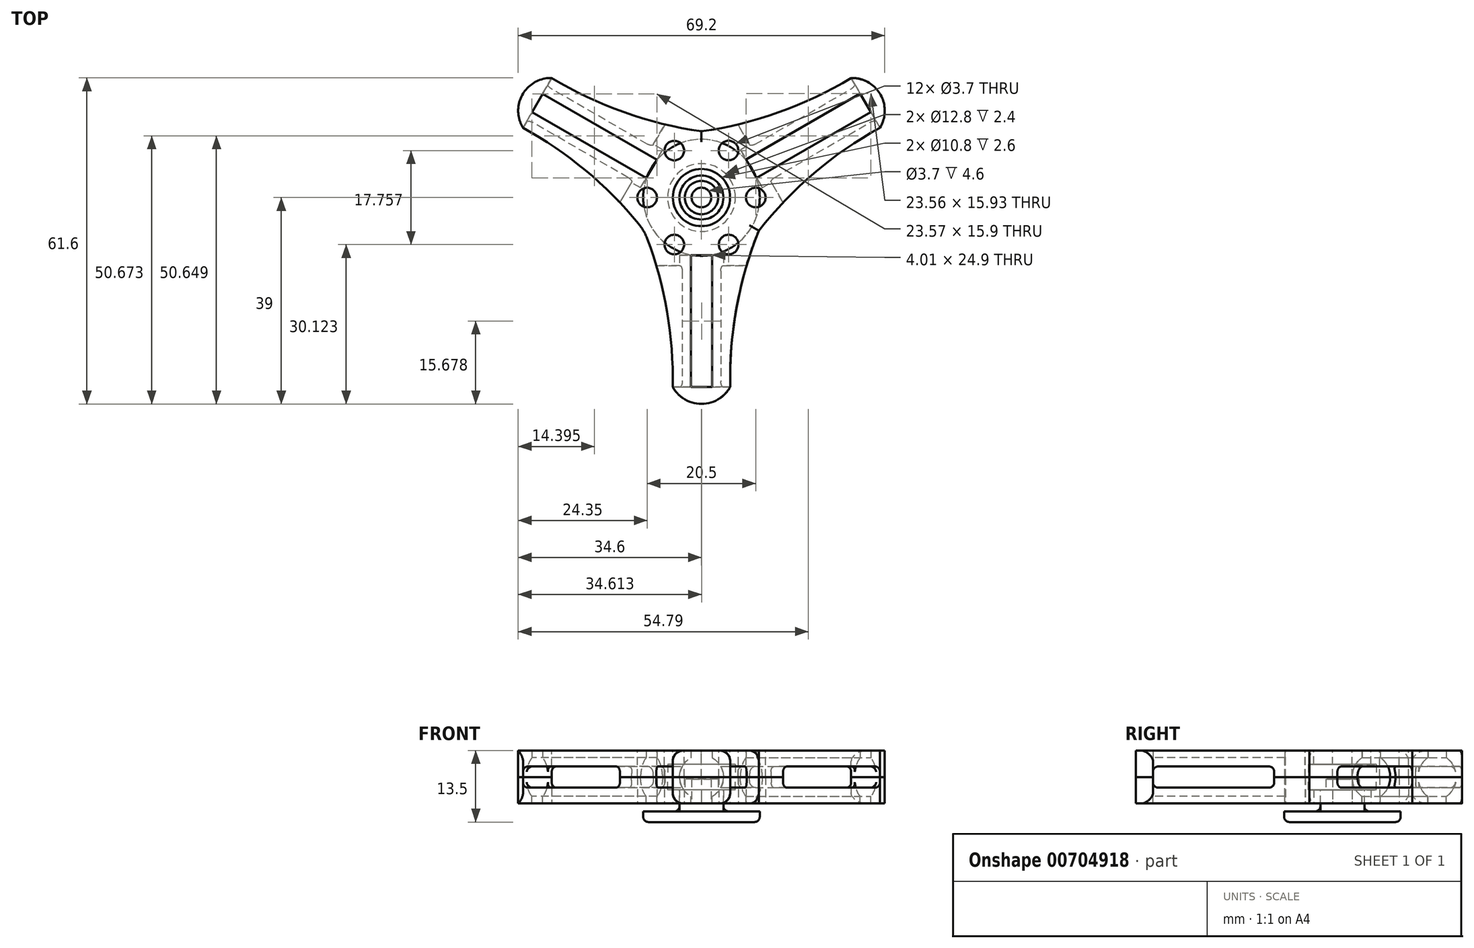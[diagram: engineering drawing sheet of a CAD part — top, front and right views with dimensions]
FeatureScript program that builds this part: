
annotation { "Feature Type Name" : "Feature", "Feature Type Description" : "" }
export const myFeature = defineFeature(function(context is Context, id is Id, definition is map)
    precondition{}
    {
        {
            var Q0;
            Q0=qCreatedBy(makeId("Top.planeOp"),FACE);
            var sketch = newSketch(context, id + "F0", { "sketchPlane" : qUnion([Q0])});
            skCircle(sketch, "E0", {"center": v(0, 0) * mm, "radius": 6.4 * mm, "construction": true});
            skArc(sketch, "E1", {"start": v(0, 12.5) * mm, "mid": v(-10.83, -6.25) * mm, "end": v(10.83, -6.25) * mm, "construction": true});
            skLineSegment(sketch, "E2", {"start": v(0, 12.5) * mm, "end": v(0, 39.67) * mm, "construction": true});
            skLineSegment(sketch, "E3", {"start": v(0, 0) * mm, "end": v(33.28, -19.21) * mm, "construction": true});
            skLineSegment(sketch, "E4", {"start": v(0, 0) * mm, "end": v(33.77, 19.5) * mm, "construction": true});
            skCircle(sketch, "E5", {"center": v(13, 7.5) * mm, "radius": 4.15 * mm, "construction": true});
            skCircle(sketch, "E6", {"center": v(20.2, 11.66) * mm, "radius": 4.15 * mm, "construction": true});
            skCircle(sketch, "E7", {"center": v(27.38, 15.8) * mm, "radius": 4.15 * mm, "construction": true});
            skLineSegment(sketch, "E8", {"start": v(33.77, 19.5) * mm, "end": v(54.08, 31.22) * mm, "construction": true});
            skPoint(sketch, "E9", {"position": v(30.98, 17.88) * mm});
            skLineSegment(sketch, "E10", {"start": v(28.26, 22.59) * mm, "end": v(33.7, 13.18) * mm});
            skArc(sketch, "E11", {"start": v(0, 12.5) * mm, "mid": v(14.64, 16.12) * mm, "end": v(28.26, 22.59) * mm});
            skArc(sketch, "E12.MirrorCS", {"start": v(10.83, -6.25) * mm, "mid": v(21.28, 4.62) * mm, "end": v(33.7, 13.18) * mm});
            skArc(sketch, "E13", {"start": v(0, 12.5) * mm, "mid": v(-10.83, -6.25) * mm, "end": v(10.83, -6.25) * mm});
            skLineSegment(sketch, "E14", {"start": v(0, 0) * mm, "end": v(6.65, 11.52) * mm, "construction": true});
            skLineSegment(sketch, "E15", {"start": v(0, 0) * mm, "end": v(12.69, 0) * mm, "construction": true});
            skCircle(sketch, "E16", {"center": v(5.12, 8.88) * mm, "radius": 1.85 * mm});
            skCircle(sketch, "E17.MirrorC", {"center": v(10.25, 0) * mm, "radius": 1.85 * mm});
            skCircle(sketch, "E18", {"center": v(0, 0) * mm, "radius": 5.4 * mm});
            skSolve(sketch);
        }
        {
            var Q0;
            Q0 = qSketchRegion(id + "F0", true);
            extrude(context, id + "F1", {"entities" : qUnion([Q0]), "depth" : 10 * mm, "offsetDistance" : 25 * mm});
        }
        {
            var Q0;
            Q0=makeQuery(id+"F1.opExtrude","SWEPT_FACE",FACE,{"disambiguationData":[OSD([sQuery(id+"F0.wireOp",EDGE,"E10")])]});
            var sketch = newSketch(context, id + "F2", { "sketchPlane" : qUnion([Q0])});
            skLineSegment(sketch, "E19", {"start": v(0, 0) * mm, "end": v(0, 10) * mm, "construction": true});
            skArc(sketch, "E20", {"start": v(-2, 8.64) * mm, "mid": v(-4.15, 5) * mm, "end": v(-2, 1.36) * mm});
            skLineSegment(sketch, "E21.bottom", {"start": v(2, -6.47) * mm, "end": v(-2, -6.47) * mm});
            skLineSegment(sketch, "E21.top", {"start": v(2, 16.47) * mm, "end": v(-2, 16.47) * mm});
            skLineSegment(sketch, "E21.left", {"start": v(2, -6.47) * mm, "end": v(2, 1.36) * mm});
            skLineSegment(sketch, "E21.right", {"start": v(-2, -6.47) * mm, "end": v(-2, 1.36) * mm});
            skArc(sketch, "E22.trimOffspring", {"start": v(2, 1.36) * mm, "mid": v(4.15, 5) * mm, "end": v(2, 8.64) * mm});
            skLineSegment(sketch, "E23.trimOffspring", {"start": v(2, 8.64) * mm, "end": v(2, 16.47) * mm});
            skLineSegment(sketch, "E24.trimOffspring", {"start": v(-2, 8.64) * mm, "end": v(-2, 16.47) * mm});
            skSolve(sketch);
        }
        {
            var Q0;
            Q0 = qSketchRegion(id + "F2", true);
            extrude(context, id + "F3", {"entities" : qUnion([Q0]), "operationType" : NewBodyOperationType.REMOVE, "oppositeDirection" : true, "depth" : 24.9 * mm, "offsetDistance" : 25 * mm});
        }
        {
            var Q0;
            Q0=qCreatedBy(makeId("Top.planeOp"),FACE);
            var sketch = newSketch(context, id + "F4", { "sketchPlane" : qUnion([Q0])});
            skLineSegment(sketch, "E25.0", {"start": v(28.26, 22.59) * mm, "end": v(29.98, 19.62) * mm});
            skLineSegment(sketch, "E25.1", {"start": v(31.98, 16.15) * mm, "end": v(33.7, 13.18) * mm});
            skLineSegment(sketch, "E26", {"start": v(29.98, 19.62) * mm, "end": v(31.98, 16.15) * mm});
            skArc(sketch, "E27", {"start": v(33.7, 13.18) * mm, "mid": v(33.77, 19.5) * mm, "end": v(28.26, 22.59) * mm});
            skSolve(sketch);
        }
        {
            var Q0;
            Q0 = qSketchRegion(id + "F4", true);
            extrude(context, id + "F5", {"entities" : qUnion([Q0]), "operationType" : NewBodyOperationType.ADD, "depth" : 10 * mm, "offsetDistance" : 25 * mm});
        }
        {
            var Q0;
            Q0=makeQuery(id+"F3.boolean.opBoolean","COPY",FACE,{"derivedFrom":makeQuery(id+"F3.opExtrude","SWEPT_FACE",FACE,{"disambiguationData":[OSD([sQuery(id+"F2.wireOp",EDGE,"E24.trimOffspring")])]})});
            var sketch = newSketch(context, id + "F6", { "sketchPlane" : qUnion([Q0])});
            skLineSegment(sketch, "E28.0", {"start": v(-35.77, 8.64) * mm, "end": v(-35.77, 10) * mm});
            skLineSegment(sketch, "E29.0", {"start": v(-10.87, 8.64) * mm, "end": v(-10.87, 10) * mm});
            skLineSegment(sketch, "E30", {"start": v(-35.77, 10) * mm, "end": v(-35.77, 0) * mm, "construction": true});
            skPoint(sketch, "E31.endSnap0", {"position": v(-10.87, 9.32) * mm});
            skLineSegment(sketch, "E32", {"start": v(-35.77, 5) * mm, "end": v(-12.87, 5) * mm, "construction": true});
            skLineSegment(sketch, "E33.bottom", {"start": v(-12.87, 7) * mm, "end": v(-35.77, 7) * mm});
            skLineSegment(sketch, "E33.top", {"start": v(-12.87, 3) * mm, "end": v(-35.77, 3) * mm});
            skLineSegment(sketch, "E33.left", {"start": v(-12.87, 7) * mm, "end": v(-12.87, 3) * mm});
            skLineSegment(sketch, "E33.right", {"start": v(-35.77, 7) * mm, "end": v(-35.77, 3) * mm});
            skPoint(sketch, "E33.middle", {"position": v(-24.32, 5) * mm});
            skSolve(sketch);
        }
        {
            var Q0;
            Q0 = qSketchRegion(id + "F6", true);
            extrude(context, id + "F7", {"entities" : qUnion([Q0]), "operationType" : NewBodyOperationType.REMOVE, "endBound" : BoundingType.SYMMETRIC, "oppositeDirection" : true, "depth" : 25 * mm, "offsetDistance" : 25 * mm});
        }
        {
            var Q0;
            {var subQ0=sQuery(id+"F6.wireOp",EDGE,"E33.top");var subQ1=sQuery(id+"F6.wireOp",EDGE,"E33.right");Q0=makeQuery(id+"F7.boolean.opBoolean","COPY",EDGE,{"disambiguationData":[TD([makeQuery(id+"F1.opExtrude","SWEPT_FACE",FACE,{"disambiguationData":[OSD([sQuery(id+"F0.wireOp",EDGE,"E11")])]})])],"derivedFrom":makeQuery(id+"F7.opExtrude","SWEPT_EDGE",EDGE,{"disambiguationData":[OSD([subQ0,subQ1])]})});}
            var Q1;
            {var subQ0=sQuery(id+"F6.wireOp",EDGE,"E33.bottom");var subQ1=sQuery(id+"F6.wireOp",EDGE,"E33.right");Q1=makeQuery(id+"F7.boolean.opBoolean","COPY",EDGE,{"disambiguationData":[TD([makeQuery(id+"F1.opExtrude","SWEPT_FACE",FACE,{"disambiguationData":[OSD([sQuery(id+"F0.wireOp",EDGE,"E11")])]})])],"derivedFrom":makeQuery(id+"F7.opExtrude","SWEPT_EDGE",EDGE,{"disambiguationData":[OSD([subQ0,subQ1])]})});}
            var Q2;
            {var subQ1=sQuery(id+"F6.wireOp",EDGE,"E33.top");var subQ2=sQuery(id+"F6.wireOp",EDGE,"E33.left");Q2=makeQuery(id+"F7.boolean.opBoolean","COPY",EDGE,{"disambiguationData":[TD([makeQuery(id+"F1.opExtrude","SWEPT_FACE",FACE,{"disambiguationData":[OSD([sQuery(id+"F0.wireOp",EDGE,"E11")])]})])],"derivedFrom":makeQuery(id+"F7.opExtrude","SWEPT_EDGE",EDGE,{"disambiguationData":[OSD([subQ1,subQ2])]})});}
            var Q3;
            {var subQ0=sQuery(id+"F6.wireOp",EDGE,"E33.bottom");var subQ2=sQuery(id+"F6.wireOp",EDGE,"E33.left");Q3=makeQuery(id+"F7.boolean.opBoolean","COPY",EDGE,{"disambiguationData":[TD([makeQuery(id+"F1.opExtrude","SWEPT_FACE",FACE,{"disambiguationData":[OSD([sQuery(id+"F0.wireOp",EDGE,"E11")])]})])],"derivedFrom":makeQuery(id+"F7.opExtrude","SWEPT_EDGE",EDGE,{"disambiguationData":[OSD([subQ0,subQ2])]})});}
            var Q4;
            {var subQ0=sQuery(id+"F6.wireOp",EDGE,"E33.bottom");var subQ2=sQuery(id+"F6.wireOp",EDGE,"E33.left");Q4=makeQuery(id+"F7.boolean.opBoolean","COPY",EDGE,{"disambiguationData":[TD([makeQuery(id+"F1.opExtrude","SWEPT_FACE",FACE,{"disambiguationData":[OSD([sQuery(id+"F0.wireOp",EDGE,"E12.MirrorCS")])]})])],"derivedFrom":makeQuery(id+"F7.opExtrude","SWEPT_EDGE",EDGE,{"disambiguationData":[OSD([subQ0,subQ2])]})});}
            var Q5;
            {var subQ0=sQuery(id+"F6.wireOp",EDGE,"E33.top");var subQ2=sQuery(id+"F6.wireOp",EDGE,"E33.left");Q5=makeQuery(id+"F7.boolean.opBoolean","COPY",EDGE,{"disambiguationData":[TD([makeQuery(id+"F1.opExtrude","SWEPT_FACE",FACE,{"disambiguationData":[OSD([sQuery(id+"F0.wireOp",EDGE,"E12.MirrorCS")])]})])],"derivedFrom":makeQuery(id+"F7.opExtrude","SWEPT_EDGE",EDGE,{"disambiguationData":[OSD([subQ0,subQ2])]})});}
            var Q6;
            {var subQ0=sQuery(id+"F6.wireOp",EDGE,"E33.right");var subQ1=sQuery(id+"F6.wireOp",EDGE,"E33.bottom");Q6=makeQuery(id+"F7.boolean.opBoolean","COPY",EDGE,{"disambiguationData":[TD([makeQuery(id+"F1.opExtrude","SWEPT_FACE",FACE,{"disambiguationData":[OSD([sQuery(id+"F0.wireOp",EDGE,"E12.MirrorCS")])]})])],"derivedFrom":makeQuery(id+"F7.opExtrude","SWEPT_EDGE",EDGE,{"disambiguationData":[OSD([subQ1,subQ0])]})});}
            var Q7;
            {var subQ0=sQuery(id+"F6.wireOp",EDGE,"E33.right");var subQ1=sQuery(id+"F6.wireOp",EDGE,"E33.top");Q7=makeQuery(id+"F7.boolean.opBoolean","COPY",EDGE,{"disambiguationData":[TD([makeQuery(id+"F1.opExtrude","SWEPT_FACE",FACE,{"disambiguationData":[OSD([sQuery(id+"F0.wireOp",EDGE,"E12.MirrorCS")])]})])],"derivedFrom":makeQuery(id+"F7.opExtrude","SWEPT_EDGE",EDGE,{"disambiguationData":[OSD([subQ1,subQ0])]})});}
            fillet(context, id + "F8", {"entities" : qUnion([Q0, Q1, Q2, Q3, Q4, Q5, Q6, Q7]), "radius" : 1 * mm, "tangentPropagation" : true, "allowEdgeOverflow" : false});
        }
        {
            var Q0;
            Q0=qCreatedBy(makeId("Top.planeOp"),FACE);
            cPlane(context, id + "F9", {"entities" : qUnion([Q0]), "cplaneType" : CPlaneType.OFFSET, "offset" : 5 * mm, "width" : 150 * mm, "height" : 150 * mm});
        }
        {
            var Q0;
            Q0=qCreatedBy(id+"F9.planeOp",FACE);
            var sketch = newSketch(context, id + "F10", { "sketchPlane" : qUnion([Q0])});
            skCircle(sketch, "E34", {"center": v(0, 0) * mm, "radius": 6.4 * mm});
            skSolve(sketch);
        }
        {
            var Q0;
            Q0 = qSketchRegion(id + "F10", true);
            extrude(context, id + "F11", {"entities" : qUnion([Q0]), "operationType" : NewBodyOperationType.REMOVE, "endBound" : BoundingType.SYMMETRIC, "oppositeDirection" : true, "depth" : 4.8 * mm, "offsetDistance" : 25 * mm});
        }
        {
            var Q0;
            Q0=qCreatedBy(makeId("Top.planeOp"),FACE);
            var sketch = newSketch(context, id + "F12", { "sketchPlane" : qUnion([Q0])});
            skLineSegment(sketch, "E35", {"start": v(0, 0) * mm, "end": v(0, 24.73) * mm});
            skLineSegment(sketch, "E36", {"start": v(0, 24.73) * mm, "end": v(-26.87, 17.31) * mm});
            skLineSegment(sketch, "E37", {"start": v(-26.87, 17.31) * mm, "end": v(-21.25, -29.23) * mm});
            skLineSegment(sketch, "E38", {"start": v(-21.25, -29.23) * mm, "end": v(15.63, -29.23) * mm});
            skLineSegment(sketch, "E39", {"start": v(15.63, -29.23) * mm, "end": v(18.93, -10.93) * mm});
            skLineSegment(sketch, "E40", {"start": v(18.93, -10.93) * mm, "end": v(0, 0) * mm});
            skSolve(sketch);
        }
        {
            var Q0;
            Q0 = qSketchRegion(id + "F12", true);
            extrude(context, id + "F13", {"entities" : qUnion([Q0]), "operationType" : NewBodyOperationType.REMOVE, "depth" : 25 * mm, "offsetDistance" : 25 * mm});
        }
        {
            var Q0;
            Q0=qCreatedBy(id+"F9.planeOp",FACE);
            var sketch = newSketch(context, id + "F14", { "sketchPlane" : qUnion([Q0])});
            skLineSegment(sketch, "E41.bottom", {"start": v(-11.04, 33.02) * mm, "end": v(42.15, 33.02) * mm});
            skLineSegment(sketch, "E41.top", {"start": v(-11.04, -14.72) * mm, "end": v(42.15, -14.72) * mm});
            skLineSegment(sketch, "E41.left", {"start": v(-11.04, 33.02) * mm, "end": v(-11.04, -14.72) * mm});
            skLineSegment(sketch, "E41.right", {"start": v(42.15, 33.02) * mm, "end": v(42.15, -14.72) * mm});
            skSolve(sketch);
        }
        {
            var Q0;
            Q0 = qSketchRegion(id + "F14", true);
            extrude(context, id + "F15", {"entities" : qUnion([Q0]), "operationType" : NewBodyOperationType.REMOVE, "depth" : 25 * mm, "offsetDistance" : 25 * mm});
        }
        {
            var Q0;
            Q0=qCreatedBy(makeId("Right.planeOp"),FACE);
            var sketch = newSketch(context, id + "F16", { "sketchPlane" : qUnion([Q0])});
            skLineSegment(sketch, "E42", {"start": v(0, 0) * mm, "end": v(0, 38.24) * mm});
            skSolve(sketch);
        }
        {
            var Q0;
            Q0=makeQuery(id+"F1.opExtrude","SWEPT_BODY",BODY,{"disambiguationData":[OSD([sQuery(id+"F0.wireOp",EDGE,"E10"),sQuery(id+"F0.wireOp",EDGE,"E11"),sQuery(id+"F0.wireOp",EDGE,"E12.MirrorCS"),sQuery(id+"F0.wireOp",EDGE,"E13"),sQuery(id+"F0.wireOp",EDGE,"E16"),sQuery(id+"F0.wireOp",EDGE,"E17.MirrorC"),sQuery(id+"F0.wireOp",EDGE,"E18")])]});
            var Q1;
            Q1=sQuery(id+"F16.wireOp",EDGE,"E42");
            circularPattern(context, id + "F17", {"operationType" : NewBodyOperationType.ADD, "entities" : qUnion([Q0]), "axis" : qUnion([Q1]), "angle" : 360 * degree, "instanceCount" : 3, "equalSpace" : true});
        }
        {
            var Q0;
            {var subQ0=sQuery(id+"F0.wireOp",EDGE,"E13");Q0=makeQuery(id+"F17.boolean.opBoolean","MERGE",EDGE,{"derivedFrom":[makeQuery(id+"F1.opExtrude","SWEPT_EDGE",EDGE,{"disambiguationData":[OSD([sQuery(id+"F0.wireOp",EDGE,"E12.MirrorCS"),subQ0])]}),makeQuery(id+"F17.opPattern","COPY",EDGE,{"derivedFrom":makeQuery(id+"F1.opExtrude","SWEPT_EDGE",EDGE,{"disambiguationData":[OSD([sQuery(id+"F0.wireOp",EDGE,"E11"),subQ0])]}),"instanceName":"2"})]});}
            var Q1;
            {var subQ0=sQuery(id+"F0.wireOp",EDGE,"E13");Q1=makeQuery(id+"F17.boolean.opBoolean","MERGE",EDGE,{"derivedFrom":[makeQuery(id+"F1.opExtrude","SWEPT_EDGE",EDGE,{"disambiguationData":[OSD([sQuery(id+"F0.wireOp",EDGE,"E11"),subQ0])]}),makeQuery(id+"F17.opPattern","COPY",EDGE,{"derivedFrom":makeQuery(id+"F1.opExtrude","SWEPT_EDGE",EDGE,{"disambiguationData":[OSD([sQuery(id+"F0.wireOp",EDGE,"E12.MirrorCS"),subQ0])]}),"instanceName":"1"})]});}
            var Q2;
            {var subQ0=sQuery(id+"F0.wireOp",EDGE,"E13");Q2=makeQuery(id+"F17.boolean.opBoolean","MERGE",EDGE,{"derivedFrom":[makeQuery(id+"F17.opPattern","COPY",EDGE,{"derivedFrom":makeQuery(id+"F1.opExtrude","SWEPT_EDGE",EDGE,{"disambiguationData":[OSD([sQuery(id+"F0.wireOp",EDGE,"E11"),subQ0])]}),"instanceName":"1"}),makeQuery(id+"F17.opPattern","COPY",EDGE,{"derivedFrom":makeQuery(id+"F1.opExtrude","SWEPT_EDGE",EDGE,{"disambiguationData":[OSD([sQuery(id+"F0.wireOp",EDGE,"E12.MirrorCS"),subQ0])]}),"instanceName":"2"})]});}
            fillet(context, id + "F18", {"entities" : qUnion([Q0, Q1, Q2]), "radius" : 10 * mm, "tangentPropagation" : true, "allowEdgeOverflow" : false});
        }
        {
            var Q0;
            Q0=makeQuery(id+"F17.opPattern","COPY",EDGE,{"derivedFrom":makeQuery(id+"F1.opExtrude","CAP_EDGE",EDGE,{"disambiguationData":[OSD([sQuery(id+"F0.wireOp",EDGE,"E12.MirrorCS")])],"isStart":true}),"instanceName":"2"});
            var Q1;
            Q1=makeQuery(id+"F17.opPattern","COPY",EDGE,{"derivedFrom":makeQuery(id+"F1.opExtrude","CAP_EDGE",EDGE,{"disambiguationData":[OSD([sQuery(id+"F0.wireOp",EDGE,"E11")])],"isStart":true}),"instanceName":"2"});
            var Q2;
            Q2=makeQuery(id+"F1.opExtrude","CAP_EDGE",EDGE,{"disambiguationData":[OSD([sQuery(id+"F0.wireOp",EDGE,"E11")])],"isStart":true});
            fillet(context, id + "F19", {"entities" : qUnion([Q0, Q1, Q2]), "radius" : 2 * mm, "tangentPropagation" : true, "allowEdgeOverflow" : false});
        }
        {
            var Q0;
            {var subQ0=makeQuery(id+"F11.boolean.opBoolean","COPY",FACE,{"derivedFrom":makeQuery(id+"F11.opExtrude","CAP_FACE",FACE,{"disambiguationData":[OSD([sQuery(id+"F10.wireOp",EDGE,"E34")])],"isStart":false})});Q0=makeQuery(id+"F17.boolean.opBoolean","MERGE",FACE,{"derivedFrom":[subQ0,makeQuery(id+"F17.opPattern","COPY",FACE,{"derivedFrom":subQ0,"instanceName":"1"}),makeQuery(id+"F17.opPattern","COPY",FACE,{"derivedFrom":subQ0,"instanceName":"2"})]});}
            var sketch = newSketch(context, id + "F20", { "sketchPlane" : qUnion([Q0])});
            skCircle(sketch, "E43", {"center": v(0, 0) * mm, "radius": 3.15 * mm});
            skSolve(sketch);
        }
        {
            var Q0;
            Q0 = qSketchRegion(id + "F20", true);
            var Q1;
            Q1 = qConstructionFilter(qBodyType(qCreatedBy(id + "F20" ,EDGE), BodyType.WIRE), ConstructionObject.NO);
            extrude(context, id + "F21", {"entities" : qUnion([Q0]), "surfaceEntities" : qUnion([Q1]), "depth" : 2 * mm, "offsetDistance" : 25 * mm});
        }
        {
            var Q0;
            {var subQ0=makeQuery(id+"F11.boolean.opBoolean","COPY",FACE,{"derivedFrom":makeQuery(id+"F11.opExtrude","CAP_FACE",FACE,{"disambiguationData":[OSD([sQuery(id+"F10.wireOp",EDGE,"E34")])],"isStart":false})});Q0=makeQuery(id+"F17.boolean.opBoolean","MERGE",FACE,{"derivedFrom":[subQ0,makeQuery(id+"F17.opPattern","COPY",FACE,{"derivedFrom":subQ0,"instanceName":"1"}),makeQuery(id+"F17.opPattern","COPY",FACE,{"derivedFrom":subQ0,"instanceName":"2"})]});}
            var sketch = newSketch(context, id + "F22", { "sketchPlane" : qUnion([Q0])});
            skCircle(sketch, "E44", {"center": v(0, 0) * mm, "radius": 4.15 * mm});
            skSolve(sketch);
        }
        {
            var Q0;
            Q0 = qSketchRegion(id + "F22", true);
            extrude(context, id + "F23", {"entities" : qUnion([Q0]), "oppositeDirection" : true, "depth" : (2.6 + 1.5) * mm, "offsetDistance" : 25 * mm});
        }
        {
            var Q0;
            Q0=makeQuery(id+"F23.opExtrude","CAP_FACE",FACE,{"disambiguationData":[OSD([sQuery(id+"F22.wireOp",EDGE,"E44")])],"isStart":false});
            var sketch = newSketch(context, id + "F24", { "sketchPlane" : qUnion([Q0])});
            skCircle(sketch, "E45", {"center": v(0, 0) * mm, "radius": 11 * mm});
            skSolve(sketch);
        }
        {
            var Q0;
            Q0 = qSketchRegion(id + "F24", true);
            extrude(context, id + "F25", {"entities" : qUnion([Q0]), "operationType" : NewBodyOperationType.ADD, "depth" : 2 * mm, "offsetDistance" : 25 * mm});
        }
        {
            var Q0;
            Q0=makeQuery(id+"F25.opExtrude","CAP_EDGE",EDGE,{"disambiguationData":[OSD([sQuery(id+"F24.wireOp",EDGE,"E45")])],"isStart":false});
            fillet(context, id + "F26", {"entities" : qUnion([Q0]), "radius" : 1 * mm, "tangentPropagation" : true, "allowEdgeOverflow" : false});
        }
        {
            var Q0;
            Q0=qCreatedBy(makeId("Right.planeOp"),FACE);
            var sketch = newSketch(context, id + "F27", { "sketchPlane" : qUnion([Q0])});
            skLineSegment(sketch, "E46", {"start": v(0, 0) * mm, "end": v(0, 11.27) * mm, "construction": true});
            skLineSegment(sketch, "E47", {"start": v(-3.15, 4.6) * mm, "end": v(-3.15, 2.6) * mm});
            skLineSegment(sketch, "E48.0", {"start": v(-5.4, 2.6) * mm, "end": v(5.4, 2.6) * mm, "construction": true});
            skLineSegment(sketch, "E49", {"start": v(-3.15, 4.6) * mm, "end": v(-1.85, 4.6) * mm});
            skLineSegment(sketch, "E50", {"start": v(-4.15, -1.5) * mm, "end": v(-11, -1.5) * mm});
            skLineSegment(sketch, "E51", {"start": v(-11, -1.5) * mm, "end": v(-11, -3.5) * mm});
            skLineSegment(sketch, "E52", {"start": v(-11, -3.5) * mm, "end": v(0, -3.5) * mm});
            skLineSegment(sketch, "E53", {"start": v(-1.85, 4.6) * mm, "end": v(-1.85, 0) * mm});
            skLineSegment(sketch, "E54", {"start": v(-1.85, 0) * mm, "end": v(0, 0) * mm});
            skLineSegment(sketch, "E55", {"start": v(0, 0) * mm, "end": v(0, -3.5) * mm});
            skLineSegment(sketch, "E56", {"start": v(-3.15, 2.6) * mm, "end": v(-4.15, 2.6) * mm});
            skLineSegment(sketch, "E57", {"start": v(-4.15, 2.6) * mm, "end": v(-4.15, -1.5) * mm});
            skSolve(sketch);
        }
        {
            var Q0;
            Q0 = qSketchRegion(id + "F27", true);
            var Q1;
            Q1=sQuery(id+"F27.wireOp",EDGE,"E46");
            revolve(context, id + "F28", {"surfaceOperationType" : NewSurfaceOperationType.NEW, "entities" : qUnion([Q0]), "axis" : qUnion([Q1]), "revolveType" : RevolveType.FULL});
        }
        {
            var Q0;
            Q0=makeQuery(id+"F28.opRevolve","SWEPT_EDGE",EDGE,{"disambiguationData":[OSD([sQuery(id+"F27.wireOp",EDGE,"E51"),sQuery(id+"F27.wireOp",EDGE,"E52")])]});
            var Q1;
            Q1=makeQuery(id+"F28.opRevolve","SWEPT_EDGE",EDGE,{"disambiguationData":[OSD([sQuery(id+"F27.wireOp",EDGE,"E50"),sQuery(id+"F27.wireOp",EDGE,"E57")])]});
            fillet(context, id + "F29", {"entities" : qUnion([Q0, Q1]), "radius" : 1 * mm, "tangentPropagation" : true, "allowEdgeOverflow" : false});
        }
        {
            var Q0;
            Q0=makeQuery(id+"F1.opExtrude","SWEPT_BODY",BODY,{"disambiguationData":[OSD([sQuery(id+"F0.wireOp",EDGE,"E10"),sQuery(id+"F0.wireOp",EDGE,"E11"),sQuery(id+"F0.wireOp",EDGE,"E12.MirrorCS"),sQuery(id+"F0.wireOp",EDGE,"E13"),sQuery(id+"F0.wireOp",EDGE,"E16"),sQuery(id+"F0.wireOp",EDGE,"E17.MirrorC"),sQuery(id+"F0.wireOp",EDGE,"E18")])]});
            var Q1;
            Q1=qCreatedBy(id+"F9.planeOp",FACE);
            mirror(context, id + "F30", {"operationType" : NewBodyOperationType.ADD, "entities" : qUnion([Q0]), "mirrorPlane" : qUnion([Q1])});
        }
    });
